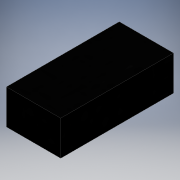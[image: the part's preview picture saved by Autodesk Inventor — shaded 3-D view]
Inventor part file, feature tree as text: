
AUTODESK INVENTOR PART (.ipt)
format: ipt  version: 2016 (Build 200138000, 138)  size: 87,040 bytes
history: native  units: mm
features: extrude x1, sketch x1
ambient origin geometry x8: Origin, YZ Plane, XZ Plane, XY Plane, X Axis, Y Axis, Z Axis, Center Point
bodies: Solid1 (feature_tree)
feature tree (2):
  extrude  "Extrusion1"  Depth=25.0mm
  sketch  "Sketch1"  dims[d0=52.0mm d1=25.0mm d2=16.0mm d3=0.0mm]
